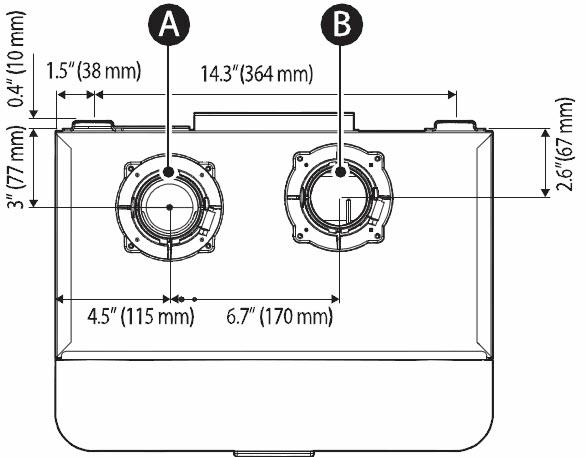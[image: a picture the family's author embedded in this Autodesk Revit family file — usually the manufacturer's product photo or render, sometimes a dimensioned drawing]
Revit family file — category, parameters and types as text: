
# Revit family: Water_Heater-Racks-Navien-NPE-10_Unit_Front-Wall-02
name_source: partatom
category: Mechanical Equipment
revit_build: Autodesk Revit 2016 (Build: 20150220_1215(x64)
units: mm (PartAtom-declared; Revit-internal decimal feet)

## family parameters
Cut with Voids When Loaded = No
Host = Face
OmniClass Number = 23.65.35.11
OmniClass Title = Supply Water Heaters
Part Type = Normal
Room Calculation Point = No
Round Connector Dimension = Use Diameter
Shared = No

## types (4) — shared parameters
2" Exhaust/Intake = Yes
3" Exhaust/Intake = No
Apparent Load = 0 VA
Assembly Code = D3010500
Certifications = Energy Star | AHRI | CSA | CSA | NFS
Cold Water Inlet = 1"
Configuration = NPE_F10_3F2F_3F2F
Default Elevation = 48 "
Depth = 23.8 "
Description = 10 Unit Front
Exhaust = 2"
Finish = Metal - Navien - White
Flow Rate = 1 GPM
Flow Rate Note = 35°F (19°C) temp rise: 11.2 GPM (42 L/m) | 45°F (25°C) temp rise: 8.7 GPM (33 L/m) | 67°F (36°C) temp rise: NPE-240A: 5.6 GPM(21 L/m), NPE-240S: 5.7 GPM(22 L/m)
Frequency = 60 Hz
Gas Inlet = 1"
Heating Capacity = 120000.0 Btu/h
Heating Capacity Note = 19,900–199,900 (BTU/H)
Height = 65.5 "
Hot Water Outlet = 1"
Ignition = Electronic ignition
Installation Type = Indoor
Intake = 2"
Keynote = 22 33 00.A1
Manifold(s) = (2) 30019040A + (2) 30019041A
Manufacturer = Navien, Inc.
Manufacturer Fax Number = (949) 420-0430
Natural Gas Manifold Pressure = -0.05" WC to -0.58" WC
Natural Gas Supply Pressure = 3.5"–10.5" WC
Number of Poles = 1
Phase = 1
Power Factor = 1
Product Documentation Link = https://www.navieninc.com
Product Name = NPE Series Tankless Water Heaters w/ Racks
Product Page URL = https://www.navieninc.com
Propane Gas Manifold Pressure = -0.10" WC to -0.78" WC
Propane Gas Supply Pressure = 8"–13" WC
Required Cascade Operation Accessory = (10) 30014367A (Common Vent Damper & Cascade Communication Cable) or (9) GXXX000546 (Individual Vent Cascade Communication Cable)
URL = https://www.navieninc.com
Venting = Exhaust: 2" PVC, CPVC, PP, SS / 2" special gas vent type BH (Class II, A/B/C) | Intake: 2" PVC, CPVC, PP, SS / 2" special gas vent type BH (Class II, A/B/C) | Vent clearances: 0" to combustibles
Venting Type = Forced draft direct vent
Version = 2016 - v1.0.a
Voltage = 120 V
Water Pressure = 15–150 PSI
Wi-Fi Ready = NaviLink Wi-Fi Control: PBCM-AS-001
Width = 23.3 "

## per-type parameters (varying)
| type | Constraints | Model | Natural Gas | Propane Gas | Recirculation Inlet | Recirculation Inlet Visibility | Tankless Water Heaters | Weight |
| Natural Gas - Recirculating System - NPE-240A(Advanced)-NG | 6 | (10) NPE-240A-NG | Yes | No | 0" | Yes | (10) NPE-240A-NG | 82.00 lbf |
| Natural Gas - NPE-240S(Standard)-NG | 7 | (10) NPE-240S-NG | Yes | No | 1" | No | (10) NPE-240S-NG | 75.00 lbf |
| Propane Gas - Recirculating System - NPE-240A(Advanced)-LPG | 6 | (10) NPE-240A-LPG | No | Yes | 0" | Yes | (10) NPE-240A-LPG | 82.00 lbf |
| Propane Gas - NPE-240S(Standard)-LPG | 7 | (10) NPE-240S-LPG | No | Yes | 1" | No | (10) NPE-240S-LPG | 75.00 lbf |

## geometry (parser evidence)
native form markers: Sweep x10
no freeform markers — native parametric forms only
